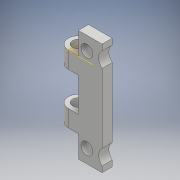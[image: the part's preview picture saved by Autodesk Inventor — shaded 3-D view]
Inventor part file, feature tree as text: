
AUTODESK INVENTOR PART (.ipt)
format: ipt  version: 2017 (Build 210142000, 142)  size: 180,224 bytes
history: native  units: mm
features: extrude x7, sketch x7, plane x1, mirror x1, projected_geometry x1
ambient origin geometry x8: Origin, YZ Plane, XZ Plane, XY Plane, X Axis, Y Axis, Z Axis, Center Point
bodies: Solid1 (feature_tree)
feature tree (17):
  extrude  "Extrusion1"  Depth=10.0mm
  plane  "Work Plane1"
  extrude  "Extrusion4"  [1 undecoded]
  extrude  "Extrusion5"  Depth=6.5mm
  extrude  "Extrusion6"  Depth=5.0mm
  extrude  "Extrusion8"  Depth=5.0mm
  mirror  "Mirror2"
  extrude  "Extrusion9"  Depth=4.0mm
  extrude  "Extrusion10"  Depth=10.0mm
  sketch  "Sketch2"  dims[d2=10.0mm d3=16.5mm]
  sketch  "Sketch5"  dims[d4=3.0mm d5=0.0mm d9=-6.5mm]
  sketch  "Sketch6"  dims[d14=6.5mm d15=0.0mm d16=6.0mm]
  sketch  "Sketch7"  dims[d18=5.0mm d19=0.0mm d20=3.5mm]
  projected_geometry  "Projected Loop1"
  sketch  "Sketch9"  dims[d21=5.0mm d22=0.0mm d28=3.5mm]
  sketch  "Sketch10"  dims[d29=4.5mm d30=4.0mm]
  sketch  "Sketch11"  dims[d31=5.0mm d32=0.0mm d33=6.0mm d34=6.0mm d35=2.0mm d36=4.0mm d37=4.0mm d38=10.0mm d39=0.0mm d40=2.0mm d41=6.0mm d42=6.0mm d43=3.0mm d44=6.0mm d45=6.0mm d46=10.0mm d47=0.0mm]
note: 1 required parameter value undecoded (feature->parameter linkage not recoverable at this tier; creation-order binding heuristic only, values carry confidence <= 0.55)
